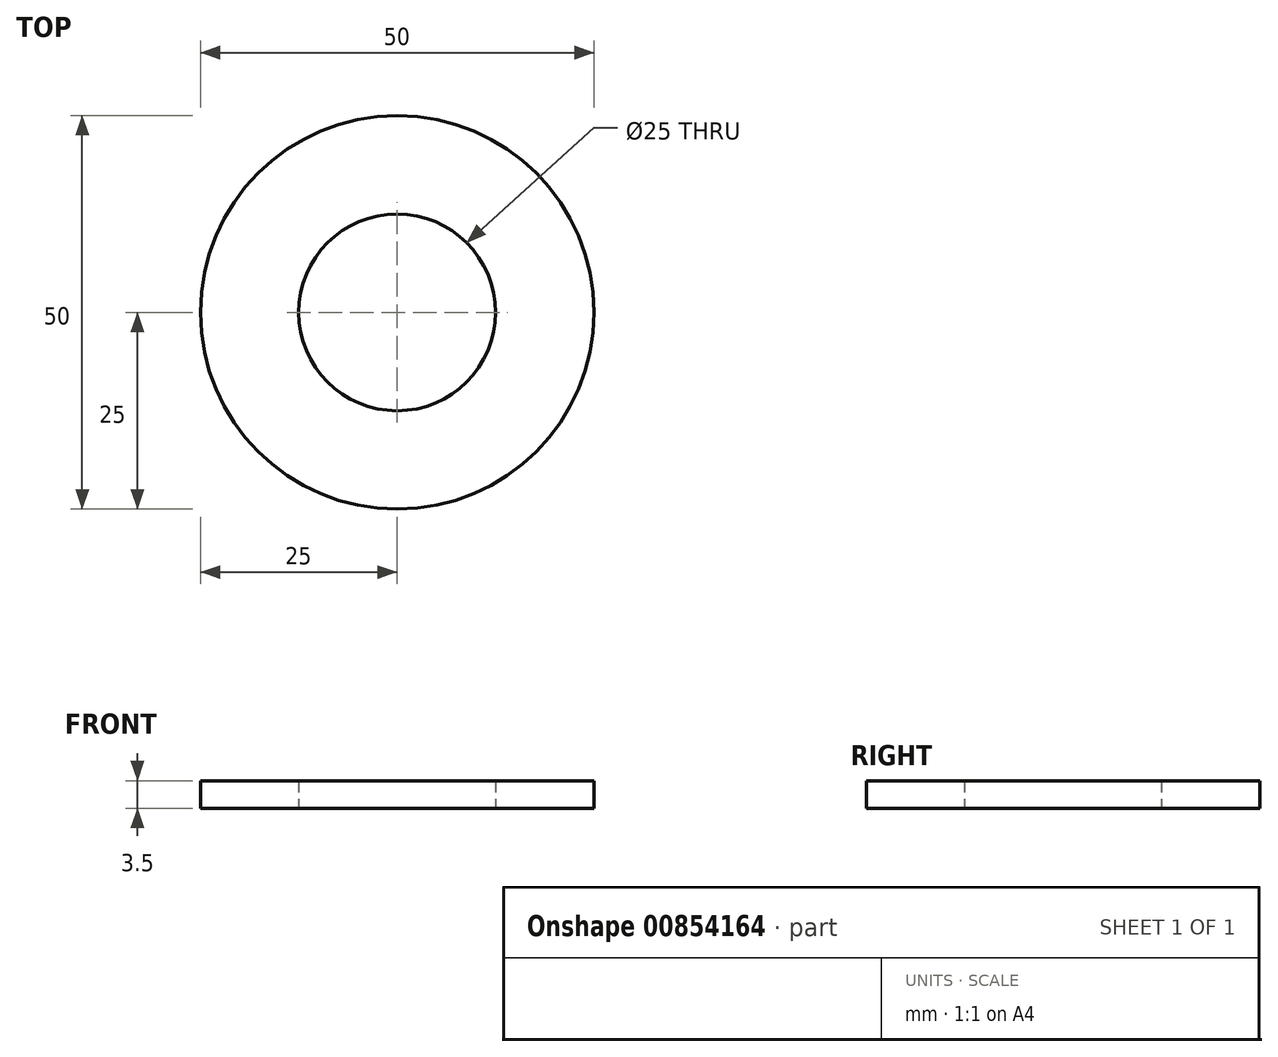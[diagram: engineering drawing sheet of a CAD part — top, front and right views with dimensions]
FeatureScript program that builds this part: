
annotation { "Feature Type Name" : "Feature", "Feature Type Description" : "" }
export const myFeature = defineFeature(function(context is Context, id is Id, definition is map)
    precondition{}
    {
        {
            var Q0;
            Q0=qCreatedBy(makeId("Top.planeOp"),FACE);
            var sketch = newSketch(context, id + "F0", { "sketchPlane" : qUnion([Q0])});
            skCircle(sketch, "E0", {"center": v(0, 0) * mm, "radius": 12.5 * mm});
            skCircle(sketch, "E1", {"center": v(0, 0) * mm, "radius": 25 * mm});
            skSolve(sketch);
        }
        {
            var Q0;
            Q0=makeQuery(id+"F0.imprint","IMPRINT",FACE,{"disambiguationData":[TD([[makeQuery(id+"F0.imprint","IMPRINT",EDGE,{"derivedFrom":sQuery(id+"F0.wireOp",EDGE,"E0")}),-1.0]])]});
            extrude(context, id + "F1", {"entities" : qUnion([Q0]), "depth" : 3.5 * mm, "offsetDistance" : 25 * mm});
        }
    });
